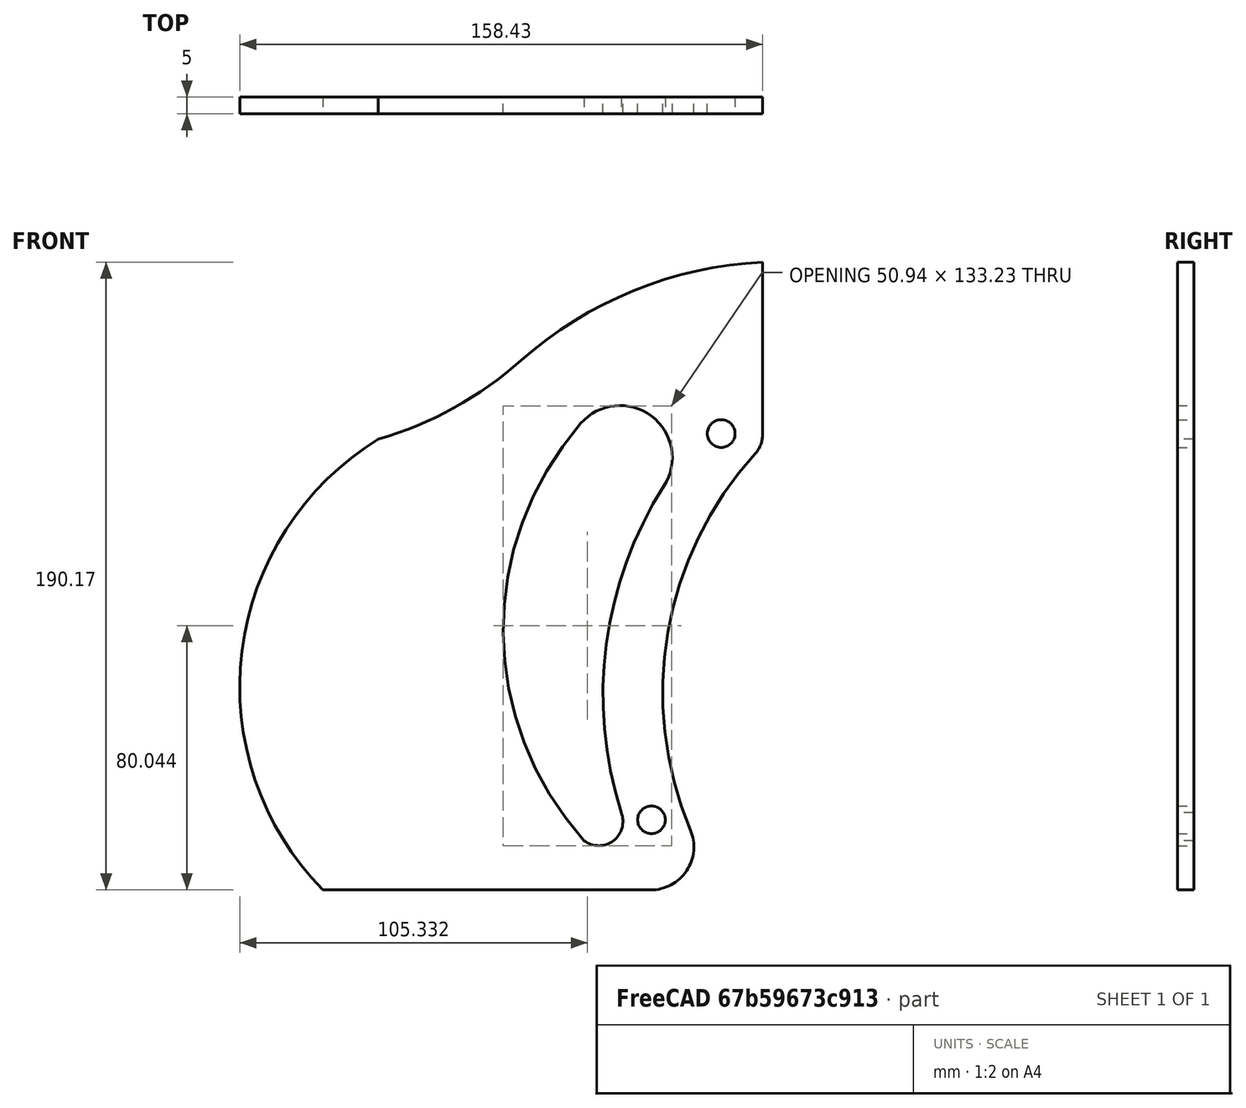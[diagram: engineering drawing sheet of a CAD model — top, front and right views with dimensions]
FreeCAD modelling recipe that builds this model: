
FCSTD DOCUMENT  (FreeCAD 0.20R29177 (Git))
Label: ButtonBox
License: All rights reserved
LicenseURL: http://en.wikipedia.org/wiki/All_rights_reserved
objects: Sketcher::SketchObject×4, Image::ImagePlane×1, PartDesign::Pad×1, PartDesign::Body×1
note: 7 computed .brp shape members not serialized (recipe doc carries the construction recipe); baked Part::Feature solids carry a one-line shape summary decoded from their .brp

FEATURE [Sketcher::SketchObject] Sketch
  FullyConstrained = false
  MapMode = 5
  Placement = pos=(0,0,0) rot=(1,0,0;1.5708rad)
  Support = -> [XZ_Plane]
  sketch-geometry (15):
    g0: ArcOfCircle CenterX=-58.0884 CenterY=-5.84198 CenterZ=0 NormalX=0 NormalY=0 NormalZ=1 AngleXU=0 Radius=95.2412 StartAngle=2.42381 EndAngle=3.87504
    g1: Circle CenterX=-108.43 CenterY=-63.2857 CenterZ=0 NormalX=0 NormalY=0 NormalZ=1 AngleXU=0 Radius=4.19854
    g2: LineSegment StartX=-74.7605 StartY=53.4216 StartZ=0 EndX=-74.7605 EndY=105.633 EndZ=0
    g3: ArcOfCircle CenterX=-68.9914 CenterY=-13.3126 CenterZ=0 NormalX=0 NormalY=0 NormalZ=1 AngleXU=0 Radius=119.085 StartAngle=1.61926 EndAngle=2.29541
    g4: ArcOfCircle CenterX=-222.849 CenterY=160.487 CenterZ=0 NormalX=0 NormalY=0 NormalZ=1 AngleXU=0 Radius=113.033 StartAngle=4.99622 EndAngle=5.437
    g5: LineSegment StartX=-108.653 StartY=-84.5382 StartZ=0 EndX=-208.043 EndY=-84.5382 EndZ=0
    g6: ArcOfCircle CenterX=-145.278 CenterY=-22.9869 CenterZ=0 NormalX=0 NormalY=0 NormalZ=1 AngleXU=0 Radius=87.9094 StartAngle=2.12038 EndAngle=3.91722
    g7: ArcOfCircle CenterX=-5.4393 CenterY=-25.4532 CenterZ=0 NormalX=0 NormalY=0 NormalZ=1 AngleXU=0 Radius=117.692 StartAngle=2.57311 EndAngle=3.44916
    g8: GeomPoint X=-97.0037 Y=41.6529 Z=0
    g9: ArcOfCircle CenterX=-124.389 CenterY=-63.8058 CenterZ=0 NormalX=0 NormalY=0 NormalZ=1 AngleXU=0 Radius=7.30652 StartAngle=4.05734 EndAngle=6.66491
    g10: ArcOfCircle CenterX=-108.653 CenterY=-71.4836 CenterZ=0 NormalX=0 NormalY=0 NormalZ=1 AngleXU=0 Radius=13.0546 StartAngle=4.71239 EndAngle=6.68127
    g11: ArcOfCircle CenterX=-117.932 CenterY=46.4109 CenterZ=0 NormalX=0 NormalY=0 NormalZ=1 AngleXU=0 Radius=15.7957 StartAngle=5.7147 EndAngle=8.70699
    g12: ArcOfCircle CenterX=2.49369 CenterY=-24.7426 CenterZ=0 NormalX=0 NormalY=0 NormalZ=1 AngleXU=0 Radius=107.521 StartAngle=2.40271 EndAngle=3.53967
    g13: ArcOfCircle CenterX=-83.3031 CenterY=53.4216 CenterZ=0 NormalX=0 NormalY=0 NormalZ=1 AngleXU=0 Radius=8.54264 StartAngle=5.54431 EndAngle=6.28319
    g14: Circle CenterX=-87.3088 CenterY=53.7 CenterZ=0 NormalX=0 NormalY=0 NormalZ=1 AngleXU=0 Radius=4.19854
  constraints (20):
    c: DistanceX(g1,g-1) = 108.43
    c: Vertical(g2)
    c: Coincident(g3,g2)
    c: Tangent(g4,g3) = 1.5708
    c: Horizontal(g5)
    c: Coincident(g6,g4)
    c: Coincident(g6,g5)
    c: DistanceX(g0,g-1) = 129.83
    c: DistanceX(g0,g-1) = 128.84
    c: DistanceY(g-1,g0) = 56.8
    c: DistanceY(g0,g-1) = 69.6
    c: Coincident(g9,g7)
    c: Coincident(g9,g0)
    c: Tangent(g5,g10) = 1.5708
    c: Tangent(g11,g0) = -1.5708
    c: Tangent(g7,g11) = 1.5708
    c: Tangent(g12,g10) = 1.5708
    c: Tangent(g13,g12) = 1.5708
    c: Tangent(g13,g2) = -1.5708
    c: Equal(g14,g1)
FEATURE [Sketcher::SketchObject] Sketch010  label="sk_mount_plate001"
  AttachmentOffset = pos=(0,48.7,0) rot=(0,0,1;0rad)
  FullyConstrained = true
  MapMode = 5
  Placement = pos=(0,-1.08e-14,48.7) rot=(1,0,0;1.5708rad)
  Support = -> [XZ_Plane]
  sketch-geometry (14):
    g0: Circle CenterX=-28 CenterY=0 CenterZ=0 NormalX=0 NormalY=0 NormalZ=1 AngleXU=0 Radius=3
    g1: Circle CenterX=28 CenterY=0 CenterZ=0 NormalX=0 NormalY=0 NormalZ=1 AngleXU=0 Radius=3
    g2: Circle CenterX=-50 CenterY=0 CenterZ=0 NormalX=0 NormalY=0 NormalZ=1 AngleXU=0 Radius=5
    g3: Circle CenterX=50 CenterY=0 CenterZ=0 NormalX=0 NormalY=0 NormalZ=1 AngleXU=0 Radius=5
    g4: LineSegment StartX=-50 StartY=0 StartZ=0 EndX=50 EndY=0 EndZ=0
    g5: ArcOfCircle CenterX=1.69e-14 CenterY=-69 CenterZ=0 NormalX=0 NormalY=0 NormalZ=1 AngleXU=0 Radius=100 StartAngle=1.21654 EndAngle=1.92505
    g6: ArcOfCircle CenterX=106.026 CenterY=217.668 CenterZ=0 NormalX=0 NormalY=0 NormalZ=1 AngleXU=0 Radius=205.647 StartAngle=4.35814 EndAngle=4.64413
    g7: GeomPoint X=0 Y=31 Z=0
    g8: LineSegment StartX=28 StartY=0 StartZ=0 EndX=28 EndY=27 EndZ=0
    g9: LineSegment StartX=50 StartY=0 StartZ=0 EndX=50 EndY=19.8 EndZ=0
    g10: ArcOfCircle CenterX=-106.026 CenterY=217.668 CenterZ=0 NormalX=0 NormalY=0 NormalZ=1 AngleXU=0 Radius=205.647 StartAngle=4.78065 EndAngle=5.06664
    g11: LineSegment StartX=-50 StartY=0 StartZ=0 EndX=-50 EndY=19.8 EndZ=0
    g12: LineSegment StartX=-92 StartY=12.5 StartZ=0 EndX=-92 EndY=0 EndZ=0
    g13: LineSegment StartX=92 StartY=12.5 StartZ=0 EndX=92 EndY=0 EndZ=0
  constraints (39):
    c: DistanceX(g0,g1) = 56  'mount_holes_distance'
    c: Symmetric(g0,g1,g-2)
    c: Equal(g0,g1)
    c: Diameter(g0) = 6  'mount_holes_diameter'
    c: Equal(g2,g3)
    c: Diameter(g2) = 10  'motor_mount_holes_diameter'
    c: Symmetric(g2,g3,g-2)
    c: Coincident(g4,g2)
    c: Coincident(g4,g3)
    c: PointOnObject(g0,g4)
    c: PointOnObject(g-1,g4)
    c: Symmetric(g5,g5,g-2)
    c: Coincident(g6,g5)
    c: PointOnObject(g7,g5)
    c: PointOnObject(g7,g-2)
    c: DistanceY(g-1,g7) = 31
    c: Coincident(g8,g1)
    c: PointOnObject(g8,g5)
    c: Vertical(g8)
    c: Coincident(g9,g3)
    c: PointOnObject(g9,g6)
    c: Vertical(g9)
    c: DistanceY(g1,g8) = 27
    c: DistanceX(g2,g3) = 100
    c: DistanceY(g9,g9) = 19.8
    c: Coincident(g11,g2)
    c: PointOnObject(g11,g10)
    c: Vertical(g11)
    c: DistanceY(g11,g11) = 19.8
    c: Symmetric(g6,g10,g-2)
    c: Coincident(g12,g10)
    c: PointOnObject(g12,g-1)
    c: Vertical(g12)
    c: DistanceY(g12,g12) = 12.5
    c: DistanceX(g12,g-1) = 92
    c: Tangent(g10,g5) = 1.5708
    c: Coincident(g13,g6)
    c: PointOnObject(g13,g-1)
    c: Vertical(g13)
FEATURE [Image::ImagePlane] ImagePlane
  Placement = pos=(1.3,50,4) rot=(-1,0,0;4.71239rad)
  XSize = 322.629
  YSize = 168.092
FEATURE [Sketcher::SketchObject] Sketch011
  AttachmentOffset = pos=(0,-5,5) rot=(0,0,1;0rad)
  ExternalGeometry = -> [Sketch]
  FullyConstrained = false
  MapMode = 5
  Placement = pos=(0,-5,-5) rot=(1,0,0;1.5708rad)
  Support = -> [XZ_Plane]
  sketch-geometry (9):
    g0: Circle CenterX=-138.027 CenterY=73.1105 CenterZ=0 NormalX=0 NormalY=0 NormalZ=1 AngleXU=0 Radius=8
    g1: Circle CenterX=-156.645 CenterY=55.9262 CenterZ=0 NormalX=0 NormalY=0 NormalZ=1 AngleXU=0 Radius=8
    g2: Circle CenterX=-179.547 CenterY=45.0907 CenterZ=0 NormalX=0 NormalY=0 NormalZ=1 AngleXU=0 Radius=8
    g3: Circle CenterX=-171.494 CenterY=-37.826 CenterZ=0 NormalX=0 NormalY=0 NormalZ=1 AngleXU=0 Radius=8
    g4: Circle CenterX=-172.985 CenterY=19.7384 CenterZ=0 NormalX=0 NormalY=0 NormalZ=1 AngleXU=0 Radius=8
    g5: Circle CenterX=-199.53 CenterY=19.7384 CenterZ=0 NormalX=0 NormalY=0 NormalZ=1 AngleXU=0 Radius=8
    g6: Circle CenterX=-199.828 CenterY=-12.4738 CenterZ=0 NormalX=0 NormalY=0 NormalZ=1 AngleXU=0 Radius=8
    g7: Circle CenterX=-170.897 CenterY=-12.7721 CenterZ=0 NormalX=0 NormalY=0 NormalZ=1 AngleXU=0 Radius=8
    g8: Circle CenterX=-198.039 CenterY=-36.3347 CenterZ=0 NormalX=0 NormalY=0 NormalZ=1 AngleXU=0 Radius=8
  constraints (9):
    c: Diameter(g0) = 16
    c: Equal(g0,g1)
    c: Equal(g1,g2)
    c: Equal(g2,g4)
    c: Equal(g4,g5)
    c: Equal(g5,g6)
    c: Equal(g6,g7)
    c: Equal(g7,g8)
    c: Equal(g8,g3)
FEATURE [Sketcher::SketchObject] Sketch012
  AttachmentOffset = pos=(0,0,5) rot=(0,0,1;0rad)
  ExternalGeometry = -> [Sketch011]
  FullyConstrained = false
  MapMode = 5
  Placement = pos=(0,-5,-1.1e-15) rot=(1,0,0;1.5708rad)
  Support = -> [XZ_Plane]
  sketch-geometry (6):
    g0: Circle CenterX=-151.51 CenterY=58.2846 CenterZ=0 NormalX=0 NormalY=0 NormalZ=1 AngleXU=0 Radius=9.75
    g1: Circle CenterX=-170.824 CenterY=41.9518 CenterZ=0 NormalX=0 NormalY=0 NormalZ=1 AngleXU=0 Radius=9.75
    g2: Circle CenterX=-193.88 CenterY=31.5468 CenterZ=0 NormalX=0 NormalY=0 NormalZ=1 AngleXU=0 Radius=9.75
    g3: Circle CenterX=-202.433 CenterY=-64.8063 CenterZ=0 NormalX=0 NormalY=0 NormalZ=1 AngleXU=0 Radius=9.75
    g4: Circle CenterX=-177.224 CenterY=-62.731 CenterZ=0 NormalX=0 NormalY=0 NormalZ=1 AngleXU=0 Radius=9.75
    g5: Circle CenterX=-153.159 CenterY=-70.52 CenterZ=0 NormalX=0 NormalY=0 NormalZ=1 AngleXU=0 Radius=9.75
  constraints (6):
    c: Equal(g5,g4)
    c: Equal(g4,g3)
    c: Equal(g3,g2)
    c: Equal(g2,g1)
    c: Equal(g1,g0)
    c: Diameter(g0) = 19.5
FEATURE [PartDesign::Pad] Pad
  Direction = (0,-1,-2e-16)
  Length = 5
  Length2 = 10
  Placement = pos=(0,0,0) rot=(1,0,0;1.5708rad)
  Profile = -> Sketch
  ReferenceAxis = -> Sketch [N_Axis]
  Refine = true
  Type = 0
FEATURE [PartDesign::Body] Body
  Group = -> [Sketch,Sketch010,Sketch011,Sketch012,Pad]
  Origin = -> Origin
  Tip = -> Pad
